# Revit family: BE_33234_de_DE
name_source: partatom
category: Leuchten
revit_build: Autodesk Revit 2015 (Build: 20150704_0715(x64)
units: mm (PartAtom-declared; Revit-internal decimal feet)

## types (4) — shared parameters
AC/DC = AC/DC
Aktualisierung = 2016-01-13T04:08:41
BEGA_Dummy = Nein
BEGA_IES = Ja
BEGA_Intern = Ja
BEGA_Intern_Konstruktion = Ja
BEGA_Intern_an = Ja
BEGA_Intern_aus = Ja
Befestigungsabstand = 220 mm
Befestigungsbohrung = Ø 5,3 mm
Beschreibung = Decken- und Wandleuchte
Beschreibung_Sonderanfertigung = Hier können Sie Informationen zur Sonderanfertigung eintragen.
CE_Konformität = ja
Energieeffizienzklasse = LED A++ - A
Farbfilter = 16777215
Farbtemperaturverschiebung bei Dämpfen der Lampe = <Keine Auswahl>
Farbwiedergabeindex = Ra > 80
Frequenz = 0/50-60 Hz
Gewicht = 5.3 kg
Hersteller = BEGA
Lampe = LED 24 W
Lastklassifizierung = Beleuchtung
Lebensdauerkriterien = L70 = 50.000 h
Logo = BEGA_Logo.png
M_W = Nein
Material_02 = BEGA_Oberfläche_Silber_matt
Material_11 = BEGA_Glas_opal
Neigungswinkel = 0.00°
Produktdatenblatt = http://www.bega.de
Scheinlast = 0 VA
Schutzart = IP 65
Schutzklasse = I
Sonderanfertigung = Nein
Spannung = 0 V
Typenbild = 33234.png
URL = http://www.bega.de
Umgebungstemperatur = 25 °C
zero-valued in all types: Vorgabe-Ansicht

## per-type parameters (varying)
| type | Bestellnummer | Datei für fotometrisches Netz | Farbtemperatur | LED_Modulbezeichnung | Lampenlichtstrom | Leuchtenlichtstrom | M_A | M_G | Modell |
| BEGA_33234_Grafit_K4 | 33234K4 | BE_33234K4.IES | 4000 K | 4x LED-0408/840 | 3300 lm | 1850 lm | Nein | Ja | 33234K4 |
| BEGA_33234_Silber_K4 | 33234AK4 | BE_33234K4.IES | 4000 K | 4x LED-0408/840 | 3300 lm | 1850 lm | Ja | Nein | 33234AK4 |
| BEGA_33234_Grafit_K3 | 33234 | BE_33234.IES | 3000 K | 4x LED-0408/830 | 3100 lm | 1738 lm | Nein | Ja | 33234 |
| BEGA_33234_Silber_K3 | 33234A | BE_33234.IES | 3000 K | 4x LED-0408/830 | 3100 lm | 1738 lm | Ja | Nein | 33234A |
